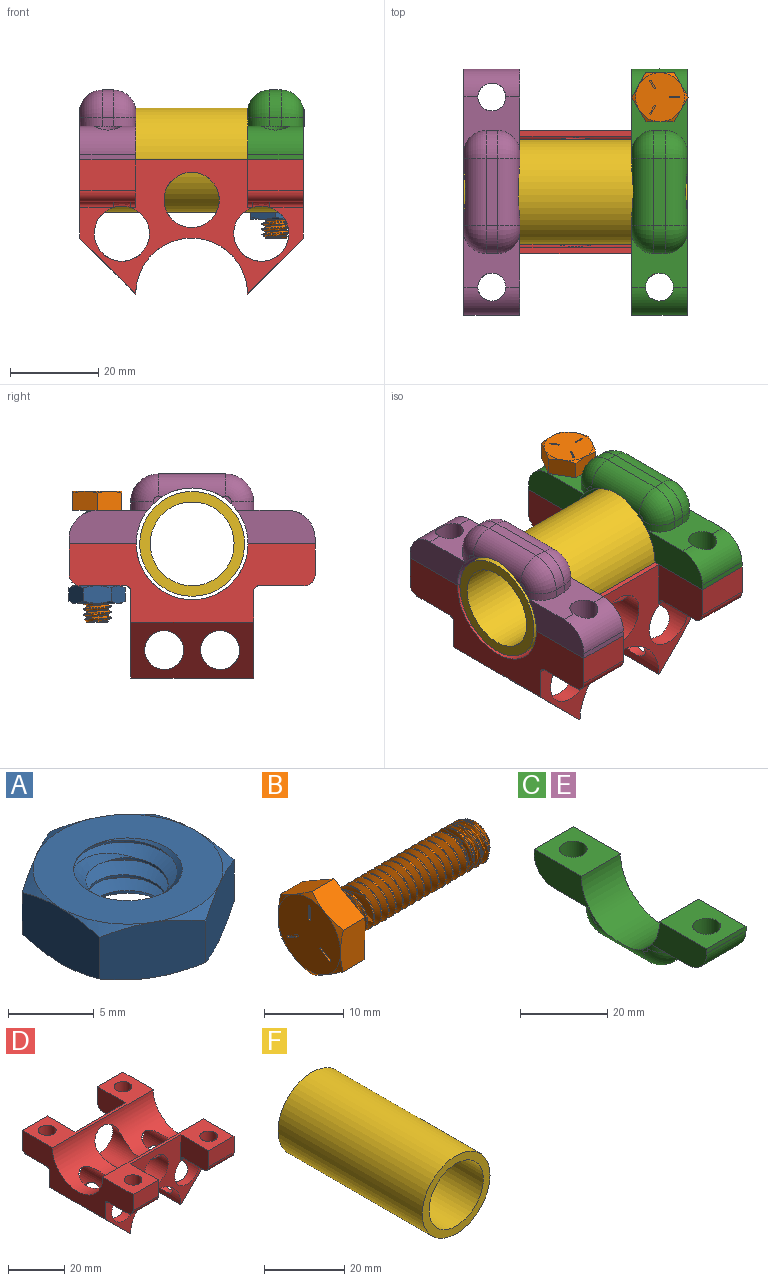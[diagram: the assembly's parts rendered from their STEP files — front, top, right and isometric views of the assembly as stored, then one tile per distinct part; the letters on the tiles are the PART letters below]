
ASSEMBLY  parts=6 mates=5
PART A: 26 faces, bbox 13.4x13.4x5.6 mm
  f0: cone r=5.56mm half-angle=60deg, axis (0,0,1), area 3mm2, adj f11,f12,f15
  f1: cone r=3.17mm half-angle=45deg, axis (0,0,-1), area 10.5mm2, adj f5,f6,f7,f15
  f2: cone r=5.56mm half-angle=60deg, axis (0,0,-1), area 3mm2, adj f8,f11,f12
  f3: cone r=3.17mm half-angle=45deg, axis (0,0,1), area 10.5mm2, adj f5,f6,f7,f8
  f4: cylinder r=3.17mm len=6.35mm, axis (0,0,-1), area 9.9mm2, adj f5,f7,f8,f15
  f5: bspline ~6.35x6.35mm, area 41.5mm2, adj f1,f3,f4,f6
  f6: bspline ~4.7x4.7mm, area 4.3mm2, adj f1,f3,f5,f7
  f7: bspline ~6.35x6.35mm, area 41.5mm2, adj f1,f3,f4,f6
  f8: plane 11.11x11.11mm, normal (0,0,1), area 65.3mm2, adj f2,f3,f4,f16,f17,f18,f19,f20
  f9: plane 6.08x4.5mm, normal (-0.5,0.87,0), area 23.3mm2, adj f10,f14,f16,f20,f23,f24
  f10: plane 6.95x4.5mm, normal (-1,0,0), area 23.3mm2, adj f9,f11,f19,f20,f24,f25
  f11: plane 6.08x4.5mm, normal (-0.5,-0.87,0), area 23.3mm2, adj f0,f2,f10,f12,f19,f25
  f12: plane 6.08x4.5mm, normal (0.5,-0.87,0), area 23.3mm2, adj f0,f2,f11,f13,f18,f21
  f13: plane 6.95x4.5mm, normal (1,0,0), area 23.3mm2, adj f12,f14,f17,f18,f21,f22
  f14: plane 6.08x4.5mm, normal (0.5,0.87,0), area 23.3mm2, adj f9,f13,f16,f17,f22,f23
  f15: plane 11.11x11.11mm, normal (0,0,-1), area 65.3mm2, adj f0,f1,f4,f21,f22,f23,f24,f25
  f16: cone r=5.56mm half-angle=60deg, axis (0,0,-1), area 3mm2, adj f8,f9,f14
  f17: cone r=5.56mm half-angle=60deg, axis (0,0,-1), area 3mm2, adj f8,f13,f14
  f18: cone r=5.56mm half-angle=60deg, axis (0,0,-1), area 3mm2, adj f8,f12,f13
  f19: cone r=5.56mm half-angle=60deg, axis (0,0,-1), area 3mm2, adj f8,f10,f11
  f20: cone r=5.56mm half-angle=60deg, axis (0,0,-1), area 3mm2, adj f8,f9,f10
  f21: cone r=5.56mm half-angle=60deg, axis (0,0,1), area 3mm2, adj f12,f13,f15
  f22: cone r=5.56mm half-angle=60deg, axis (0,0,1), area 3mm2, adj f13,f14,f15
  f23: cone r=5.56mm half-angle=60deg, axis (0,0,1), area 3mm2, adj f9,f14,f15
  f24: cone r=5.56mm half-angle=60deg, axis (0,0,1), area 3mm2, adj f9,f10,f15
  f25: cone r=5.56mm half-angle=60deg, axis (0,0,1), area 3mm2, adj f10,f11,f15
PART B: 35 faces, bbox 30.8x13.4x13.4 mm
  f0: cylinder r=0.17mm len=0.31mm, axis (-1,0,0), area 0.1mm2, adj f21,f32,f33,f34
  f1: cylinder r=0.17mm len=0.31mm, axis (-1,0,0), area 0.1mm2, adj f21,f27,f29,f30
  f2: cone r=2.4mm half-angle=45deg, axis (-1,0,0), area 8.9mm2, adj f3,f10,f12,f13
  f3: cylinder r=3.17mm len=24.62mm, axis (1,0,0), area 61.4mm2, adj f2,f12,f13,f14
  f4: plane 6.95x4.9mm, normal (0,-1,0), area 26.9mm2, adj f5,f9,f14,f15,f20
  f5: plane 6.08x4.89mm, normal (0,-0.5,0.87), area 26.9mm2, adj f4,f6,f14,f19,f20
  f6: plane 6.08x4.89mm, normal (0,0.5,0.87), area 26.9mm2, adj f5,f7,f14,f18,f19
  f7: plane 6.95x4.9mm, normal (0,1,0), area 26.9mm2, adj f6,f8,f14,f17,f18
  f8: plane 6.08x4.89mm, normal (0,0.5,-0.87), area 26.9mm2, adj f7,f9,f14,f16,f17
  f9: plane 6.08x4.89mm, normal (0,-0.5,-0.87), area 26.9mm2, adj f4,f8,f14,f15,f16
  f10: plane 4.81x4.79mm, normal (1,0,0), area 18mm2, adj f2,f11,f12,f13
  f11: bspline ~25.72x4.7mm, area 46.8mm2, adj f10,f12,f13,f14
  f12: bspline ~25.9x6.35mm, area 325.5mm2, adj f2,f3,f10,f11,f14
  f13: bspline ~26.35x6.35mm, area 326.3mm2, adj f2,f3,f10,f11,f14
  f14: plane 12.85x11.13mm, normal (1,0,0), area 82.7mm2, adj f3,f4,f5,f6,f7,f8,f9,f11
  f15: cone r=5.56mm half-angle=60deg, axis (1,0,0), area 3mm2, adj f4,f9,f21
  f16: cone r=5.56mm half-angle=60deg, axis (1,0,0), area 3mm2, adj f8,f9,f21
  f17: cone r=5.56mm half-angle=60deg, axis (1,0,0), area 3mm2, adj f7,f8,f21
  f18: cone r=5.56mm half-angle=60deg, axis (1,0,0), area 3mm2, adj f6,f7,f21
  f19: cone r=5.56mm half-angle=60deg, axis (1,0,0), area 3mm2, adj f5,f6,f21
  f20: cone r=5.56mm half-angle=60deg, axis (1,0,0), area 3mm2, adj f4,f5,f21
  f21: plane 11.11x11.11mm, normal (-1,0,0), area 94.8mm2, adj f0,f1,f15,f16,f17,f18,f19,f20
  f22: cylinder r=0.17mm len=0.33mm, axis (-1,0,0), area 0.1mm2, adj f21,f23,f25,f26
  f23: plane 1.89x0.25mm, normal (0,1,0), area 0.5mm2, adj f21,f22,f24,f26
  f24: cylinder r=0.17mm len=0.33mm, axis (-1,0,0), area 0.1mm2, adj f21,f23,f25,f26
  f25: plane 1.89x0.25mm, normal (0,-1,0), area 0.5mm2, adj f21,f22,f24,f26
  f26: plane 2.22x0.33mm, normal (-1,0,0), area 0.7mm2, adj f22,f23,f24,f25
  f27: plane 1.64x0.94mm, normal (0,-0.5,0.87), area 0.5mm2, adj f1,f21,f28,f30
  f28: cylinder r=0.17mm len=0.31mm, axis (-1,0,0), area 0.1mm2, adj f21,f27,f29,f30
  f29: plane 1.64x0.94mm, normal (0,0.5,-0.87), area 0.5mm2, adj f1,f21,f28,f30
  f30: plane 1.97x1.28mm, normal (-1,0,0), area 0.7mm2, adj f1,f27,f28,f29
  f31: cylinder r=0.17mm len=0.31mm, axis (-1,0,0), area 0.1mm2, adj f21,f32,f33,f34
  f32: plane 1.64x0.94mm, normal (0,-0.5,-0.87), area 0.5mm2, adj f0,f21,f31,f34
  f33: plane 1.64x0.94mm, normal (0,0.5,0.87), area 0.5mm2, adj f0,f21,f31,f34
  f34: plane 1.97x1.28mm, normal (-1,0,0), area 0.7mm2, adj f0,f31,f32,f33
PART C: 34 faces, bbox 12.7x55.9x15.9 mm
  f0: plane 17.78x7.62mm, normal (1,0,0), area 113.6mm2, adj f6,f13,f14,f17,f21
  f1: plane 17.78x7.62mm, normal (1,0,0), area 113.6mm2, adj f9,f15,f16,f17,f20
  f2: plane 2.2x1.73mm, normal (1,0,0), area 1.4mm2, adj f17,f31,f32,f33
  f3: plane 17.78x7.62mm, normal (-1,0,0), area 113.6mm2, adj f6,f13,f14,f17,f21
  f4: plane 17.78x7.62mm, normal (-1,0,0), area 113.6mm2, adj f9,f15,f16,f17,f20
  f5: plane 2.2x1.73mm, normal (-1,0,0), area 1.4mm2, adj f17,f24,f25,f26
  f6: plane 15.24x12.7mm, normal (0,0,1), area 161.9mm2, adj f0,f3,f13,f17,f19
  f7: plane 2.2x1.73mm, normal (-1,0,0), area 1.4mm2, adj f17,f26,f27,f28
  f8: plane 2.2x1.73mm, normal (1,0,0), area 1.4mm2, adj f17,f29,f30,f31
  f9: plane 15.24x12.7mm, normal (0,0,1), area 161.9mm2, adj f1,f4,f15,f17,f18
  f10: plane 15.24x2.54mm, normal (0,0,-1), area 38.7mm2, adj f22,f23,f26,f31
  f11: plane 2.54x1.91mm, normal (0,-1,0), area 4.8mm2, adj f14,f23,f28,f33
  f12: plane 2.54x1.91mm, normal (0,1,0), area 4.8mm2, adj f16,f22,f24,f29
  f13: plane 12.7x1.27mm, normal (0,-1,0), area 16.1mm2, adj f0,f3,f6,f21
  f14: plane 12.7x11.43mm, normal (0,0,-1), area 91.9mm2, adj f0,f3,f11,f17,f19,f21,f28,f33
  f15: plane 12.7x1.27mm, normal (0,1,0), area 16.1mm2, adj f1,f4,f9,f20
  f16: plane 12.7x11.43mm, normal (0,0,-1), area 91.9mm2, adj f1,f4,f12,f17,f18,f20,f24,f29
  f17: cylinder r=12.7mm len=25.4mm, axis (-1,0,0), area 500.8mm2, adj f0,f1,f2,f3,f4,f5,f6,f7
  f18: cylinder r=3.17mm len=7.62mm, axis (0,0,-1), area 147.8mm2, adj f9,f16,f20
  f19: cylinder r=3.17mm len=7.62mm, axis (0,0,-1), area 147.8mm2, adj f6,f14,f21
  f20: cylinder r=6.35mm len=12.7mm, axis (1,0,0), area 110.3mm2, adj f1,f4,f15,f16,f18
  f21: cylinder r=6.35mm len=12.7mm, axis (-1,0,0), area 110.3mm2, adj f0,f3,f13,f14,f19
  f22: cylinder r=6.35mm len=6.35mm, axis (1,0,0), area 25.3mm2, adj f10,f12,f25,f30
  f23: cylinder r=6.35mm len=6.35mm, axis (-1,0,0), area 25.3mm2, adj f10,f11,f27,f32
  f24: cylinder r=5.08mm len=5.08mm, axis (0,0,-1), area 14.2mm2, adj f5,f12,f16,f17,f25
  f25: torus R=1.27mm, axis (1,0,0), area 56.5mm2, adj f5,f22,f24,f26
  f26: cylinder r=5.08mm len=15.24mm, axis (0,1,0), area 104mm2, adj f5,f7,f10,f17,f25,f27
  f27: torus R=1.27mm, axis (1,0,0), area 56.5mm2, adj f7,f23,f26,f28
  f28: cylinder r=5.08mm len=5.08mm, axis (0,0,1), area 14.2mm2, adj f7,f11,f14,f17,f27
  f29: cylinder r=5.08mm len=5.08mm, axis (0,0,1), area 14.2mm2, adj f8,f12,f16,f17,f30
  f30: torus R=1.27mm, axis (-1,0,0), area 56.5mm2, adj f8,f22,f29,f31
  f31: cylinder r=5.08mm len=15.24mm, axis (0,1,0), area 104mm2, adj f2,f8,f10,f17,f30,f32
  f32: torus R=1.27mm, axis (-1,0,0), area 56.5mm2, adj f2,f23,f31,f33
  f33: cylinder r=5.08mm len=5.08mm, axis (0,0,-1), area 14.2mm2, adj f2,f11,f14,f17,f32
PART D: 49 faces, bbox 52.7x57.7x32.3 mm
  f0: cylinder r=12.7mm len=27.94mm, axis (0,1,0), area 813.7mm2, adj f3,f4,f8,f9,f25,f26,f27,f28
  f1: cylinder r=6.27mm len=27.94mm, axis (0,-1,0), area 783.1mm2, adj f3,f4,f5,f27,f28,f34,f40
  f2: cylinder r=6.27mm len=27.94mm, axis (0,-1,0), area 783.1mm2, adj f3,f4,f5,f25,f26,f37,f43
  f3: plane 50.8x30.48mm, normal (0,-1,0), area 490.4mm2, adj f0,f1,f2,f7,f8,f9,f10,f11
  f4: plane 50.8x30.48mm, normal (0,1,0), area 490.4mm2, adj f0,f1,f2,f6,f7,f8,f9,f11
  f5: cylinder r=12.7mm len=50.8mm, axis (1,0,0), area 1442.7mm2, adj f1,f2,f6,f7,f10,f11,f24
  f6: plane 50.8x15.24mm, normal (0,0,1), area 356mm2, adj f4,f5,f7,f11,f18,f19,f21,f22
  f7: plane 55.88x17.78mm, normal (1,0,0), area 507.5mm2, adj f3,f4,f5,f6,f9,f10,f16,f17
  f8: plane 27.94x12.7mm, normal (-0.71,0,-0.71), area 326.3mm2, adj f0,f3,f4,f11,f25,f26
  f9: plane 29.81x14.57mm, normal (0.71,0,-0.71), area 326.3mm2, adj f0,f3,f4,f7,f27,f28
  f10: plane 50.8x15.24mm, normal (0,0,1), area 356mm2, adj f3,f5,f7,f11,f12,f13,f15,f16
  f11: plane 55.88x17.78mm, normal (-1,0,0), area 507.5mm2, adj f3,f4,f5,f6,f8,f10,f12,f14
  f12: plane 12.7x6.99mm, normal (0,-1,0), area 88.7mm2, adj f10,f11,f13,f32
  f13: plane 13.97x10.8mm, normal (1,0,0), area 132mm2, adj f3,f10,f12,f14,f32,f42
  f14: plane 12.7x10.2mm, normal (0,0,-1), area 97.4mm2, adj f11,f13,f32,f42,f43,f44,f48
  f15: plane 13.97x10.8mm, normal (-1,0,0), area 132mm2, adj f3,f10,f16,f17,f31,f41
  f16: plane 12.7x6.99mm, normal (0,-1,0), area 88.7mm2, adj f7,f10,f15,f31
  f17: plane 12.7x10.2mm, normal (0,0,-1), area 97.4mm2, adj f7,f15,f31,f39,f40,f41,f47
  f18: plane 13.97x10.8mm, normal (1,0,0), area 132mm2, adj f4,f6,f19,f20,f29,f36
  f19: plane 12.7x6.99mm, normal (0,1,0), area 88.7mm2, adj f6,f11,f18,f29
  f20: plane 12.7x10.2mm, normal (0,0,-1), area 97.4mm2, adj f11,f18,f29,f36,f37,f38,f46
  f21: plane 13.97x10.8mm, normal (-1,0,0), area 132mm2, adj f4,f6,f22,f23,f30,f35
  f22: plane 12.7x6.99mm, normal (0,1,0), area 88.7mm2, adj f6,f7,f21,f30
  f23: plane 12.7x10.2mm, normal (0,0,-1), area 97.4mm2, adj f7,f21,f30,f33,f34,f35,f45
  f24: cylinder r=6.27mm len=27.94mm, axis (0,-1,0), area 559.3mm2, adj f3,f4,f5
  f25: cylinder r=4.45mm len=16.81mm, axis (-1,0,0), area 138.1mm2, adj f0,f2,f8
  f26: cylinder r=4.45mm len=16.81mm, axis (-1,0,0), area 138.1mm2, adj f0,f2,f8
  f27: cylinder r=4.45mm len=16.81mm, axis (-1,0,0), area 138.1mm2, adj f0,f1,f9
  f28: cylinder r=4.45mm len=16.81mm, axis (-1,0,0), area 138.1mm2, adj f0,f1,f9
  f29: cylinder r=2.54mm len=12.7mm, axis (1,0,0), area 50.7mm2, adj f11,f18,f19,f20
  f30: cylinder r=2.54mm len=12.7mm, axis (1,0,0), area 50.7mm2, adj f7,f21,f22,f23
  f31: cylinder r=2.54mm len=12.7mm, axis (-1,0,0), area 50.7mm2, adj f7,f15,f16,f17
  f32: cylinder r=2.54mm len=12.7mm, axis (-1,0,0), area 50.7mm2, adj f11,f12,f13,f14
  f33: cylinder r=1.27mm len=7.66mm, axis (-1,0,0), area 15.3mm2, adj f4,f7,f23,f34
  f34: bspline ~4.9x1.62mm, area 6.8mm2, adj f1,f23,f33,f35
  f35: cylinder r=1.27mm len=1.27mm, axis (-1,0,0), area 2.5mm2, adj f4,f21,f23,f34
  f36: cylinder r=1.27mm len=1.27mm, axis (-1,0,0), area 2.5mm2, adj f4,f18,f20,f37
  f37: bspline ~4.9x1.62mm, area 6.8mm2, adj f2,f20,f36,f38
  f38: cylinder r=1.27mm len=7.66mm, axis (-1,0,0), area 15.3mm2, adj f4,f11,f20,f37
  f39: cylinder r=1.27mm len=7.66mm, axis (1,0,0), area 15.3mm2, adj f3,f7,f17,f40
  f40: bspline ~4.9x1.62mm, area 6.8mm2, adj f1,f17,f39,f41
  f41: cylinder r=1.27mm len=1.27mm, axis (1,0,0), area 2.5mm2, adj f3,f15,f17,f40
  f42: cylinder r=1.27mm len=1.27mm, axis (1,0,0), area 2.5mm2, adj f3,f13,f14,f43
  f43: bspline ~4.9x1.62mm, area 6.8mm2, adj f2,f14,f42,f44
  f44: cylinder r=1.27mm len=7.66mm, axis (1,0,0), area 15.3mm2, adj f3,f11,f14,f43
  f45: cylinder r=3.17mm len=9.53mm, axis (0,0,1), area 190mm2, adj f6,f23
  f46: cylinder r=3.17mm len=9.53mm, axis (0,0,1), area 190mm2, adj f6,f20
  f47: cylinder r=3.17mm len=9.53mm, axis (0,0,1), area 190mm2, adj f10,f17
  f48: cylinder r=3.17mm len=9.53mm, axis (0,0,1), area 190mm2, adj f10,f14
PART E: same geometry as C
PART F: 4 faces, bbox 23.8x50.8x23.8 mm
  f0: cylinder r=9.53mm len=50.8mm, axis (0,1,0), area 3040.2mm2, adj f2,f3
  f1: cylinder r=11.91mm len=50.8mm, axis (0,1,0), area 3800.3mm2, adj f2,f3
  f2: plane 23.81x23.81mm, normal (0,-1,0), area 160.3mm2, adj f0,f1
  f3: plane 23.81x23.81mm, normal (0,1,0), area 160.3mm2, adj f0,f1
PLACE A rot(axis=(1,0,0),0deg) t=(-106.54,29.06,15.36)mm
PLACE B rot(axis=(0,1,0),90deg) t=(-106.43,29.02,23.97)mm
PLACE C rot(axis=(1,0,0),180deg) t=(-87.49,-6.5,52.27)mm
PLACE D rot(axis=(1,0,0),0deg) t=(-125.59,21.44,-3.61)mm
PLACE E rot(axis=(1,0,0),180deg) t=(-125.59,-6.5,52.27)mm
PLACE F rot(axis=(0.58,0.58,-0.58),120deg) t=(-125.59,7.47,26.87)mm
MATE fastened B.f14 <-> C.f19  axis (0,0,-1) through (-106.54,29.06,34.49)mm
MATE fastened D.f47 <-> C.f18  axis (0,0,1) through (-106.54,-14.12,26.87)mm
MATE fastened A.f0 <-> D.f45  axis (0,0,1) through (-106.54,29.06,17.34)mm
MATE fastened F.f0 <-> D.f5  axis (1,0,0) through (-125.59,7.47,26.87)mm
MATE fastened E.f18 <-> D.f48  axis (0,0,-1) through (-144.64,-14.12,26.87)mm
